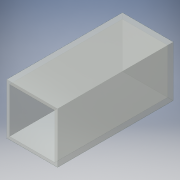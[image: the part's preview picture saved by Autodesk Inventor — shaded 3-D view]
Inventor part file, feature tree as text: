
AUTODESK INVENTOR PART (.ipt)
format: ipt  version: 2016 (Build 200138000, 138)  size: 103,424 bytes
history: native  units: mm
features: extrude x2, sketch x2
ambient origin geometry x8: Origin, YZ Plane, XZ Plane, XY Plane, X Axis, Y Axis, Z Axis, Center Point
bodies: Solid1 (feature_tree)
feature tree (4):
  extrude  "Extrusion1"  Depth=45.0mm
  extrude  "Extrusion2"  Depth=40.0mm
  sketch  "Sketch1"  dims[d0=45.0mm d1=45.0mm]
  sketch  "Sketch2"  dims[d2=40.0mm d3=40.0mm d4=100.0mm d5=0.0mm d6=2.5mm d7=0.0mm]
